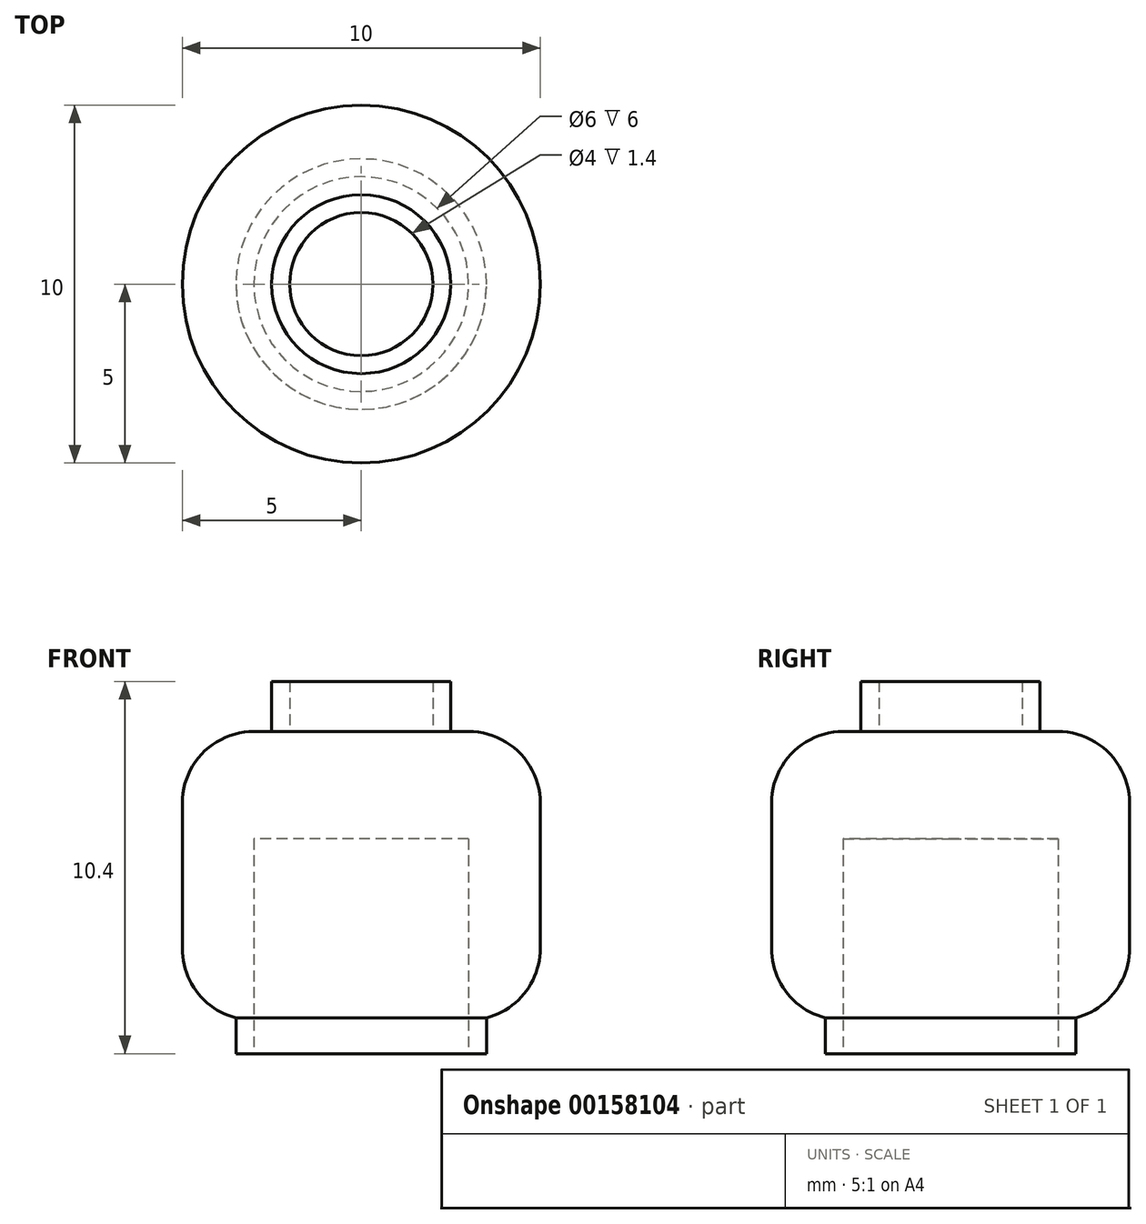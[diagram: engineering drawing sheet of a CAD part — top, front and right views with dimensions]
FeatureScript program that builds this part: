
annotation { "Feature Type Name" : "Feature", "Feature Type Description" : "" }
export const myFeature = defineFeature(function(context is Context, id is Id, definition is map)
    precondition{}
    {
        {
            var Q0;
            Q0=qCreatedBy(makeId("Top.planeOp"),FACE);
            var sketch = newSketch(context, id + "F0", { "sketchPlane" : qUnion([Q0])});
            skCircle(sketch, "E0", {"center": v(0, 0) * mm, "radius": 3.5 * mm});
            skCircle(sketch, "E1", {"center": v(0, 0) * mm, "radius": 3 * mm});
            skSolve(sketch);
        }
        {
            var Q0;
            Q0=makeQuery(id+"F0.imprint","IMPRINT",FACE,{"disambiguationData":[TD([[makeQuery(id+"F0.imprint","IMPRINT",EDGE,{"derivedFrom":sQuery(id+"F0.wireOp",EDGE,"E0")}),1.0]])]});
            extrude(context, id + "F1", {"entities" : qUnion([Q0]), "depth" : 1 * mm});
        }
        {
            var Q0;
            Q0=makeQuery(id+"F1.opExtrude","CAP_FACE",FACE,{"disambiguationData":[OSD([sQuery(id+"F0.wireOp",EDGE,"E0"),sQuery(id+"F0.wireOp",EDGE,"E1")])],"isStart":false});
            var sketch = newSketch(context, id + "F2", { "sketchPlane" : qUnion([Q0])});
            skCircle(sketch, "E2", {"center": v(0, 0) * mm, "radius": 5 * mm});
            skSolve(sketch);
        }
        {
            var Q0;
            Q0=makeQuery(id+"F2.imprint","IMPRINT",FACE,{"disambiguationData":[TD([[makeQuery(id+"F2.imprint","IMPRINT",EDGE,{"derivedFrom":makeQuery(id+"F1.opExtrude","CAP_EDGE",EDGE,{"disambiguationData":[OSD([sQuery(id+"F0.wireOp",EDGE,"E0")])],"isStart":false})}),1.0]])]});
            var Q1;
            Q1=makeQuery(id+"F2.imprint","IMPRINT",FACE,{"disambiguationData":[TD([[makeQuery(id+"F2.imprint","IMPRINT",EDGE,{"derivedFrom":sQuery(id+"F2.wireOp",EDGE,"E2")}),1.0]])]});
            var Q2;
            Q2=makeQuery(id+"F2.imprint","IMPRINT",FACE,{"disambiguationData":[TD([[makeQuery(id+"F2.imprint","IMPRINT",EDGE,{"derivedFrom":makeQuery(id+"F1.opExtrude","CAP_EDGE",EDGE,{"disambiguationData":[OSD([sQuery(id+"F0.wireOp",EDGE,"E1")])],"isStart":false})}),1.0]])]});
            extrude(context, id + "F3", {"entities" : qUnion([Q0, Q1, Q2]), "operationType" : NewBodyOperationType.ADD, "depth" : 8 * mm});
        }
        {
            var Q0;
            Q0=makeQuery(id+"F3.opExtrude","CAP_FACE",FACE,{"disambiguationData":[OSD([sQuery(id+"F2.wireOp",EDGE,"E2")])],"isStart":false});
            var sketch = newSketch(context, id + "F4", { "sketchPlane" : qUnion([Q0])});
            skCircle(sketch, "E3", {"center": v(0, 0) * mm, "radius": 2.5 * mm});
            skCircle(sketch, "E4", {"center": v(0, 0) * mm, "radius": 2 * mm});
            skSolve(sketch);
        }
        {
            var Q0;
            Q0=makeQuery(id+"F4.imprint","IMPRINT",FACE,{"disambiguationData":[TD([[makeQuery(id+"F4.imprint","IMPRINT",EDGE,{"derivedFrom":sQuery(id+"F4.wireOp",EDGE,"E3")}),1.0]])]});
            extrude(context, id + "F5", {"entities" : qUnion([Q0]), "operationType" : NewBodyOperationType.ADD, "depth" : 1.4 * mm});
        }
        {
            var Q0;
            Q0=makeQuery(id+"F3.opExtrude","CAP_EDGE",EDGE,{"disambiguationData":[OSD([sQuery(id+"F2.wireOp",EDGE,"E2")])],"isStart":false});
            var Q1;
            Q1=makeQuery(id+"F3.opExtrude","CAP_EDGE",EDGE,{"disambiguationData":[OSD([sQuery(id+"F2.wireOp",EDGE,"E2")])],"isStart":true});
            fillet(context, id + "F6", {"entities" : qUnion([Q0, Q1]), "radius" : 2 * mm, "tangentPropagation" : true, "allowEdgeOverflow" : false});
        }
        {
            var Q0;
            Q0=makeQuery(id+"F3.boolean.opBoolean","SPLIT",FACE,{"disambiguationData":[TD([makeQuery(id+"F1.opExtrude","SWEPT_FACE",FACE,{"disambiguationData":[OSD([sQuery(id+"F0.wireOp",EDGE,"E1")])]})])],"derivedFrom":makeQuery(id+"F3.opExtrude","CAP_FACE",FACE,{"disambiguationData":[OSD([sQuery(id+"F2.wireOp",EDGE,"E2")])],"isStart":true})});
            extrude(context, id + "F7", {"entities" : qUnion([Q0]), "operationType" : NewBodyOperationType.REMOVE, "oppositeDirection" : true, "depth" : 5 * mm});
        }
    });
